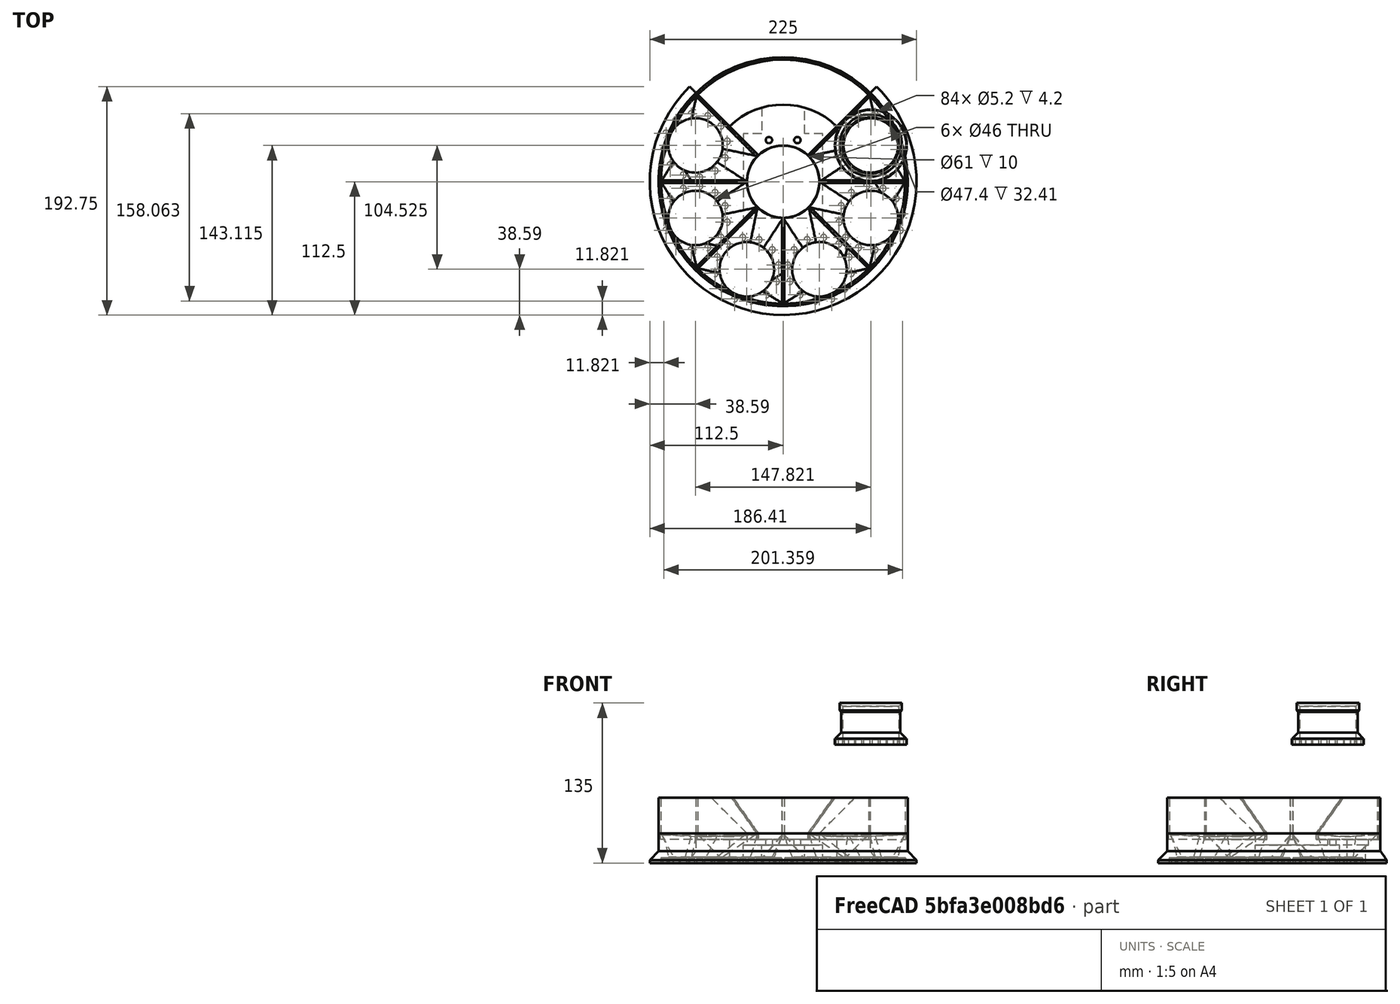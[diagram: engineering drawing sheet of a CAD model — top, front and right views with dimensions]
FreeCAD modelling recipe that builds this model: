
FCSTD DOCUMENT  (FreeCAD 1.0R38806 (Git))
Label: Dust Collector Hose Sorter - Magnetic
License: All rights reserved
LicenseURL: https://en.wikipedia.org/wiki/All_rights_reserved
objects: Sketcher::SketchObject×19, PartDesign::Pocket×9, PartDesign::Pad×7, PartDesign::Chamfer×4, PartDesign::PolarPattern×3, PartDesign::Body×3, Mesh::Feature×2, PartDesign::Groove×1, PartDesign::SubtractiveLoft×1, PartDesign::Boolean×1
note: 115 computed .brp shape members not serialized (recipe doc carries the construction recipe); baked Part::Feature solids carry a one-line shape summary decoded from their .brp

FEATURE [Sketcher::SketchObject] Sketch
  ArcFitTolerance = 1e-06
  AttachmentSupport = -> [XY_Plane]
  FullyConstrained = true
  MakeInternals = false
  MapMode = 5
  sketch-geometry (2):
    g0: Circle CenterX=0 CenterY=0 CenterZ=0 NormalX=0 NormalY=0 NormalZ=1 AngleXU=0 Radius=105
    g1: Circle CenterX=0 CenterY=0 CenterZ=0 NormalX=0 NormalY=0 NormalZ=1 AngleXU=0 Radius=30.5
  constraints (4):
    c: Coincident(g0,g-1)
    c: Diameter(g1) = 61
    c: Coincident(g1,g0)
    c: Diameter(g0) = 210
FEATURE [Sketcher::SketchObject] Sketch012  label="ArmCutout"
  ArcFitTolerance = 1e-06
  FullyConstrained = false
  MakeInternals = false
  MapMode = 5
  sketch-geometry (12):
    g0: LineSegment StartX=33.5 StartY=-30.5 StartZ=0 EndX=33.5 EndY=40.5 EndZ=0
    g1: LineSegment StartX=33.5 StartY=40.5 StartZ=0 EndX=18 EndY=40.5 EndZ=0
    g2: LineSegment StartX=-33.5 StartY=40.5 StartZ=0 EndX=-33.5 EndY=-30.5 EndZ=0
    g3: LineSegment StartX=-33.5 StartY=-30.5 StartZ=0 EndX=33.5 EndY=-30.5 EndZ=0
    g4: GeomPoint [constr] X=0 Y=0 Z=0
    g5: Circle [constr] CenterX=-12 CenterY=35.1 CenterZ=0 NormalX=0 NormalY=0 NormalZ=1 AngleXU=0 Radius=2.7
    g6: Circle [constr] CenterX=12 CenterY=35.1 CenterZ=0 NormalX=0 NormalY=0 NormalZ=1 AngleXU=0 Radius=2.7
    g7: LineSegment StartX=18 StartY=40.5 StartZ=0 EndX=18 EndY=183.45 EndZ=0
    g8: LineSegment StartX=18 StartY=183.45 StartZ=0 EndX=-18 EndY=183.45 EndZ=0
    g9: LineSegment StartX=-18 StartY=183.45 StartZ=0 EndX=-18 EndY=40.5 EndZ=0
    g10: GeomPoint [constr] X=1e-16 Y=15.8458 Z=0
    g11: LineSegment StartX=-18 StartY=40.5 StartZ=0 EndX=-33.5 EndY=40.5 EndZ=0
  constraints (28):
    c: Coincident(g0,g1)
    c: Coincident(g11,g2)
    c: Coincident(g2,g3)
    c: Coincident(g3,g0)
    c: Vertical(g0)
    c: Vertical(g2)
    c: Horizontal(g3)
    c: Coincident(g4,g-1)
    c: DistanceX(g11,g1) = 67
    c: DistanceY(g0,g0) = 71
    c: DistanceY(g2,g4) = 30.5
    c: Symmetric(g11,g0,g-2)
    c: Diameter(g5) = 5.4
    c: Diameter(g6) = 5.4
    c: DistanceX(g5,g6) = 24
    c: DistanceY(g4,g5) = 35.1
    c: Symmetric(g5,g6,g-2)
    c: Coincident(g7,g8)
    c: Coincident(g8,g9)
    c: Vertical(g7)
    c: Vertical(g9)
    c: Horizontal(g8)
    c: PointOnObject(g10,g-2)
    c: DistanceX(g8,g8) = 36
    c: PointOnObject(g9,g11)
    c: Coincident(g1,g7)
    c: PointOnObject(g11,g9)
    c: Symmetric(g9,g1,g-2)
FEATURE [Sketcher::SketchObject] Sketch017  label="ScrewHoles"
  ArcFitTolerance = 1e-06
  FullyConstrained = true
  MakeInternals = false
  MapMode = 5
  sketch-geometry (7):
    g0: LineSegment [constr] StartX=33.5 StartY=-30.5 StartZ=0 EndX=33.5 EndY=40.5 EndZ=0
    g1: LineSegment [constr] StartX=33.5 StartY=40.5 StartZ=0 EndX=-33.5 EndY=40.5 EndZ=0
    g2: LineSegment [constr] StartX=-33.5 StartY=40.5 StartZ=0 EndX=-33.5 EndY=-30.5 EndZ=0
    g3: LineSegment [constr] StartX=-33.5 StartY=-30.5 StartZ=0 EndX=33.5 EndY=-30.5 EndZ=0
    g4: GeomPoint [constr] X=0 Y=0 Z=0
    g5: Circle CenterX=-12 CenterY=35.1 CenterZ=0 NormalX=0 NormalY=0 NormalZ=1 AngleXU=0 Radius=2.7
    g6: Circle CenterX=12 CenterY=35.1 CenterZ=0 NormalX=0 NormalY=0 NormalZ=1 AngleXU=0 Radius=2.7
  constraints (17):
    c: Coincident(g0,g1)
    c: Coincident(g1,g2)
    c: Coincident(g2,g3)
    c: Coincident(g3,g0)
    c: Vertical(g0)
    c: Vertical(g2)
    c: Horizontal(g3)
    c: Coincident(g4,g-1)
    c: DistanceX(g1,g1) = 67
    c: DistanceY(g0,g0) = 71
    c: DistanceY(g2,g4) = 30.5
    c: Symmetric(g1,g0,g-2)
    c: Diameter(g5) = 5.4
    c: Diameter(g6) = 5.4
    c: DistanceX(g5,g6) = 24
    c: DistanceY(g4,g5) = 35.1
    c: Symmetric(g5,g6,g-2)
FEATURE [PartDesign::Pad] Pad  label="BaseBody"
  Direction = (0,0,1)
  Length = 25
  Length2 = 10
  Profile = -> Sketch
  ReferenceAxis = -> Sketch [N_Axis]
  Refine = true
  Suppressed = false
  Type = 0
FEATURE [PartDesign::Pocket] Pocket  label="Arm"
  BaseFeature = -> Pad
  Direction = (0,0,-1)
  Length = 15
  Length2 = 5
  Profile = -> Sketch012
  ReferenceAxis = -> Sketch012 [N_Axis]
  Refine = true
  Reversed = true
  Suppressed = false
  Type = 0
FEATURE [PartDesign::Pocket] Pocket001  label="Screws"
  BaseFeature = -> Pocket
  Direction = (0,0,-1)
  Length = 5
  Length2 = 5
  Midplane = true
  Profile = -> Sketch017
  ReferenceAxis = -> Sketch017 [N_Axis]
  Refine = true
  Suppressed = false
  Type = 1
FEATURE [Sketcher::SketchObject] Sketch027
  ArcFitTolerance = 1e-06
  AttachmentOffset = pos=(0,0,45) rot=(0,0,1;1.96349rad)
  FullyConstrained = true
  MakeInternals = false
  MapMode = 5
  Placement = pos=(0,0,25) rot=(0,0,1;1.96349rad)
  sketch-geometry (8):
    g0: Circle [constr] CenterX=0 CenterY=0 CenterZ=0 NormalX=0 NormalY=0 NormalZ=1 AngleXU=0 Radius=30.5
    g1: ArcOfCircle CenterX=0 CenterY=0 CenterZ=0 NormalX=0 NormalY=0 NormalZ=1 AngleXU=0 Radius=103 StartAngle=4.31969 EndAngle=5.10509
    g2: LineSegment [constr] StartX=0 StartY=0 StartZ=0 EndX=-39.4164 EndY=-95.1596 EndZ=0
    g3: LineSegment [constr] StartX=0 StartY=0 StartZ=0 EndX=39.4164 EndY=-95.1596 EndZ=0
    g4: LineSegment [constr] StartX=-39.4164 StartY=-95.1596 StartZ=0 EndX=39.4164 EndY=-95.1596 EndZ=0
    g5: LineSegment StartX=-11.6718 StartY=-28.1783 StartZ=0 EndX=-39.4164 EndY=-95.1596 EndZ=0
    g6: LineSegment StartX=39.4164 StartY=-95.1596 StartZ=0 EndX=11.6718 EndY=-28.1783 EndZ=0
    g7: ArcOfCircle CenterX=0 CenterY=0 CenterZ=0 NormalX=0 NormalY=0 NormalZ=1 AngleXU=0 Radius=30.5 StartAngle=4.31969 EndAngle=5.10509
  constraints (22):
    c: Diameter(g0) = 61
    c: Coincident(g0,g-1)
    c: Coincident(g1,g0)
    c: Diameter(g1) = 206
    c: Coincident(g2,g0)
    c: Coincident(g3,g0)
    c: Angle(g2,g3) = 0.785398
    c: Coincident(g4,g2)
    c: Coincident(g4,g3)
    c: Horizontal(g4)
    c: PointOnObject(g5,g0)
    c: Coincident(g5,g2)
    c: Coincident(g6,g3)
    c: PointOnObject(g6,g0)
    c: PointOnObject(g5,g2)
    c: PointOnObject(g6,g3)
    c: Coincident(g7,g0)
    c: Equal(g7,g0)
    c: PointOnObject(g7,g2)
    c: PointOnObject(g7,g3)
    c: Coincident(g1,g3)
    c: Coincident(g1,g2)
FEATURE [Sketcher::SketchObject] Sketch028
  ArcFitTolerance = 1e-06
  AttachmentSupport = -> [XZ_Plane005]
  FullyConstrained = false
  MakeInternals = false
  MapMode = 5
  Placement = pos=(0,0,0) rot=(1,0,0;1.5708rad)
  sketch-geometry (4):
    g0: LineSegment StartX=-30.5 StartY=0 StartZ=0 EndX=-103.271 EndY=72.7715 EndZ=0
    g1: LineSegment StartX=-103.271 StartY=72.7715 StartZ=0 EndX=-22.389 EndY=72.7715 EndZ=0
    g2: LineSegment StartX=-22.389 StartY=72.7715 StartZ=0 EndX=-22.389 EndY=0 EndZ=0
    g3: LineSegment StartX=-30.5 StartY=0 StartZ=0 EndX=-22.389 EndY=0 EndZ=0
  constraints (10):
    c: PointOnObject(g0,g-1)
    c: Angle(g-1,g0) = 2.35619
    c: DistanceX(g0,g-1) = 30.5
    c: Coincident(g1,g0)
    c: Horizontal(g1)
    c: Coincident(g2,g1)
    c: Vertical(g2)
    c: PointOnObject(g3,g0)
    c: Coincident(g3,g2)
    c: Horizontal(g3)
FEATURE [Sketcher::SketchObject] Sketch025
  ArcFitTolerance = 1e-06
  AttachmentOffset = pos=(0,0,-5) rot=(0,0,1;0rad)
  AttachmentSupport = -> [XY_Plane005]
  FullyConstrained = true
  MakeInternals = false
  MapMode = 5
  Placement = pos=(0,0,-5) rot=(0,0,1;0rad)
  sketch-geometry (15):
    g0: Circle [constr] CenterX=0 CenterY=0 CenterZ=0 NormalX=0 NormalY=0 NormalZ=1 AngleXU=0 Radius=30.5
    g1: Circle [constr] CenterX=0 CenterY=0 CenterZ=0 NormalX=0 NormalY=0 NormalZ=1 AngleXU=0 Radius=103.5
    g2: LineSegment [constr] StartX=0 StartY=0 StartZ=0 EndX=-31.9833 EndY=-98.4343 EndZ=0
    g3: LineSegment [constr] StartX=0 StartY=0 StartZ=0 EndX=31.9833 EndY=-98.4343 EndZ=0
    g4: LineSegment [constr] StartX=-31.9833 StartY=-98.4343 StartZ=0 EndX=31.9833 EndY=-98.4343 EndZ=0
    g5: LineSegment StartX=-10.3709 StartY=-28.6827 StartZ=0 EndX=-32.9328 EndY=-98.1207 EndZ=0
    g6: LineSegment StartX=-32.9328 StartY=-98.1207 StartZ=0 EndX=-31.0307 EndY=-98.7388 EndZ=0
    g7: LineSegment StartX=-31.0307 StartY=-98.7388 StartZ=0 EndX=-8.46877 EndY=-29.3007 EndZ=0
    g8: LineSegment StartX=-8.46877 StartY=-29.3007 StartZ=0 EndX=-10.3709 EndY=-28.6827 EndZ=0
    g9: GeomPoint X=-9.42502 Y=-29.0072 Z=0
    g10: LineSegment [constr] StartX=9.89926 StartY=-28.8488 StartZ=0 EndX=32.4584 EndY=-98.2787 EndZ=0
    g11: LineSegment [constr] StartX=32.4584 StartY=-98.2787 StartZ=0 EndX=31.5074 EndY=-98.5877 EndZ=0
    g12: LineSegment [constr] StartX=31.5074 StartY=-98.5877 StartZ=0 EndX=8.94821 EndY=-29.1578 EndZ=0
    g13: LineSegment [constr] StartX=8.94821 StartY=-29.1578 StartZ=0 EndX=9.89926 EndY=-28.8488 EndZ=0
    g14: GeomPoint [constr] X=9.42502 Y=-29.0072 Z=0
  constraints (40):
    c: Diameter(g0) = 61
    c: Coincident(g0,g-1)
    c: Diameter(g1) = 207
    c: Coincident(g1,g0)
    c: Coincident(g2,g0)
    c: PointOnObject(g2,g1)
    c: Coincident(g3,g0)
    c: PointOnObject(g3,g1)
    c: Angle(g2,g3) = 0.628319
    c: Coincident(g4,g2)
    c: Coincident(g4,g3)
    c: Horizontal(g4)
    c: Coincident(g6,g5)
    c: Coincident(g8,g7)
    c: Coincident(g8,g5)
    c: PointOnObject(g5,g0)
    c: PointOnObject(g7,g0)
    c: Coincident(g7,g6)
    c: PointOnObject(g5,g1)
    c: PointOnObject(g6,g1)
    c: Distance(g5,g6) = 2
    c: Distance(g7,g5) = 2
    c: PointOnObject(g9,g2)
    c: PointOnObject(g9,g0)
    c: Distance(g5,g9) = 1
    c: Distance(g5,g2) = 1
    c: Coincident(g11,g10)
    c: Coincident(g12,g11)
    c: Coincident(g13,g10)
    c: Distance(g12,g10) = 1
    c: Distance(g11,g10) = 1
    c: Coincident(g12,g13)
    c: PointOnObject(g10,g0)
    c: PointOnObject(g12,g0)
    c: PointOnObject(g10,g1)
    c: PointOnObject(g11,g1)
    c: PointOnObject(g14,g0)
    c: PointOnObject(g14,g3)
    c: Distance(g14,g10) = 0.5
    c: Distance(g10,g3) = 0.5
FEATURE [Sketcher::SketchObject] Sketch026
  ArcFitTolerance = 1e-06
  AttachmentSupport = -> [XY_Plane005]
  FullyConstrained = true
  MakeInternals = false
  MapMode = 5
  sketch-geometry (2):
    g0: Circle CenterX=0 CenterY=0 CenterZ=0 NormalX=0 NormalY=0 NormalZ=1 AngleXU=0 Radius=105
    g1: Circle CenterX=0 CenterY=0 CenterZ=0 NormalX=0 NormalY=0 NormalZ=1 AngleXU=0 Radius=103
  constraints (4):
    c: Diameter(g0) = 210
    c: Coincident(g0,g-1)
    c: Diameter(g1) = 206
    c: Coincident(g1,g0)
FEATURE [PartDesign::Pad] Pad005
  Direction = (0,0,1)
  Length = 30
  Length2 = 10
  Profile = -> Sketch026
  ReferenceAxis = -> Sketch026 [N_Axis]
  Refine = true
  Suppressed = false
  Type = 0
FEATURE [PartDesign::Pad] Pad006
  BaseFeature = -> Pad005
  Direction = (0,0,1)
  Length = 35
  Length2 = 10
  Profile = -> Sketch025
  ReferenceAxis = -> Sketch025 [N_Axis]
  Refine = true
  Suppressed = false
  Type = 0
FEATURE [PartDesign::PolarPattern] PolarPattern001
  Angle = 360
  Axis = -> Sketch025 [N_Axis]
  BaseFeature = -> Pad006
  Mode = 1
  Occurrences = 7
  Offset = 45
  Originals = -> [Pad006]
  Refine = true
  Suppressed = false
  TransformMode = 0
FEATURE [Sketcher::SketchObject] Sketch030
  ArcFitTolerance = 1e-06
  AttachmentOffset = pos=(0,0,0) rot=(0,0,1;-0.314159rad)
  AttachmentSupport = -> [XY_Plane005]
  FullyConstrained = false
  MakeInternals = false
  MapMode = 5
  Placement = pos=(0,0,0) rot=(0,0,1;5.96903rad)
  sketch-geometry (8):
    g0: LineSegment [constr] StartX=-109.281 StartY=0 StartZ=0 EndX=0 EndY=0 EndZ=0
    g1: LineSegment [constr] StartX=0 StartY=0 StartZ=0 EndX=-2.14e-14 EndY=-116.69 EndZ=0
    g2: LineSegment StartX=-266.815 StartY=-1 StartZ=0 EndX=-22.98 EndY=-1 EndZ=0
    g3: LineSegment StartX=-22.98 StartY=-1 StartZ=0 EndX=-1 EndY=-14.8427 EndZ=0
    g4: LineSegment StartX=-1 StartY=-14.8427 StartZ=0 EndX=-1 EndY=-153.677 EndZ=0
    g5: LineSegment [constr] StartX=-1 StartY=-14.8427 StartZ=0 EndX=-2.8e-15 EndY=-14.8427 EndZ=0
    g6: LineSegment StartX=-266.815 StartY=-1 StartZ=0 EndX=-141.723 EndY=-96.8759 EndZ=0
    g7: LineSegment StartX=-141.723 StartY=-96.8759 StartZ=0 EndX=-1 EndY=-153.677 EndZ=0
  constraints (16):
    c: PointOnObject(g0,g-1)
    c: Coincident(g0,g-1)
    c: Coincident(g1,g0)
    c: Angle(g0,g1) = 1.5708
    c: Horizontal(g2)
    c: Coincident(g3,g2)
    c: Coincident(g4,g3)
    c: Parallel(g4,g1)
    c: Coincident(g5,g3)
    c: PointOnObject(g5,g1)
    c: Angle(g4,g5) = 1.5708
    c: Distance(g3,g5) = 1
    c: DistanceY(g2,g0) = 1
    c: Coincident(g6,g2)
    c: Coincident(g7,g6)
    c: Coincident(g7,g4)
FEATURE [PartDesign::Pocket] Pocket004
  BaseFeature = -> PolarPattern001
  Direction = (0,0,-1)
  Length = 30
  Length2 = 5
  Profile = -> Sketch030
  ReferenceAxis = -> Sketch030 [N_Axis]
  Refine = true
  Reversed = true
  Suppressed = false
  Type = 0
FEATURE [PartDesign::Groove] Groove
  Angle = 360
  Angle2 = 60
  Axis = (0,2e-16,1)
  Base = (0,0,0)
  BaseFeature = -> Pocket004
  Profile = -> Sketch028
  ReferenceAxis = -> Sketch028 [V_Axis]
  Refine = true
  Reversed = true
  Suppressed = false
  Type = 0
FEATURE [Sketcher::SketchObject] Sketch031
  ArcFitTolerance = 1e-06
  AttachmentSupport = -> [XY_Plane005]
  FullyConstrained = true
  MakeInternals = false
  MapMode = 5
  sketch-geometry (1):
    g0: Circle CenterX=0 CenterY=0 CenterZ=0 NormalX=0 NormalY=0 NormalZ=1 AngleXU=0 Radius=30.5
  constraints (2):
    c: Diameter(g0) = 61
    c: Coincident(g0,g-1)
FEATURE [PartDesign::Pocket] Pocket005
  BaseFeature = -> Groove
  Direction = (0,0,-1)
  Length = 5
  Length2 = 5
  Midplane = true
  Profile = -> Sketch031
  ReferenceAxis = -> Sketch031 [N_Axis]
  Refine = true
  Suppressed = false
  Type = 1
FEATURE [PartDesign::Body] Body005  label="Splitter"
  AllowCompound = false
  Group = -> [Sketch025,Sketch026,Pad005,Pad006,PolarPattern001,Sketch030,Pocket004,Sketch028,Groove,Sketch031,Pocket005]
  Origin = -> Origin005
  Placement = pos=(0,0,25) rot=(0,0,1;-2.04203rad)
  Tip = -> Pocket005
FEATURE [Mesh::Feature] CS7_1_Sorter_Base_8_Slot_Ramp  label="CS7.1 Sorter Base 8 Slot Ramp"
  Placement = pos=(28.65,-111,29) rot=(0,0,1;0rad)
FEATURE [Sketcher::SketchObject] Sketch020
  ArcFitTolerance = 1e-06
  AttachmentOffset = pos=(0,0,5) rot=(0,0,1;1.96349rad)
  AttachmentSupport = -> [XY_Plane]
  FullyConstrained = true
  MakeInternals = false
  MapMode = 5
  Placement = pos=(0,0,5) rot=(0,0,1;1.96349rad)
  sketch-geometry (2):
    g0: Circle CenterX=0 CenterY=-80 CenterZ=0 NormalX=0 NormalY=0 NormalZ=1 AngleXU=0 Radius=23
    g1: Circle [constr] CenterX=0 CenterY=0 CenterZ=0 NormalX=0 NormalY=0 NormalZ=1 AngleXU=0 Radius=105
  constraints (5):
    c: Diameter(g0) = 46
    c: PointOnObject(g0,g-2)
    c: DistanceY(g0,g-1) = 80
    c: Diameter(g1) = 210
    c: Coincident(g1,g-1)
FEATURE [PartDesign::SubtractiveLoft] SubtractiveLoft
  BaseFeature = -> Pocket001
  Closed = false
  Profile = -> Sketch027
  Refine = true
  Ruled = true
  Sections = -> [Sketch020]
  Suppressed = false
FEATURE [Sketcher::SketchObject] Sketch034
  ArcFitTolerance = 1e-06
  AttachmentOffset = pos=(0,0,25) rot=(0,0,1;-2.35619rad)
  AttachmentSupport = -> [XY_Plane]
  FullyConstrained = false
  MakeInternals = false
  MapMode = 5
  Placement = pos=(0,0,25) rot=(0,0,1;3.92699rad)
  sketch-geometry (8):
    g0: LineSegment [constr] StartX=-109.281 StartY=0 StartZ=0 EndX=0 EndY=0 EndZ=0
    g1: LineSegment [constr] StartX=0 StartY=0 StartZ=0 EndX=-2.14e-14 EndY=-116.69 EndZ=0
    g2: LineSegment StartX=-266.815 StartY=-1 StartZ=0 EndX=-22.98 EndY=-1 EndZ=0
    g3: LineSegment StartX=-22.98 StartY=-1 StartZ=0 EndX=-1 EndY=-14.8427 EndZ=0
    g4: LineSegment StartX=-1 StartY=-14.8427 StartZ=0 EndX=-1 EndY=-153.677 EndZ=0
    g5: LineSegment [constr] StartX=-1 StartY=-14.8427 StartZ=0 EndX=-2.7e-15 EndY=-14.8427 EndZ=0
    g6: LineSegment StartX=-266.815 StartY=-1 StartZ=0 EndX=-141.723 EndY=-96.8759 EndZ=0
    g7: LineSegment StartX=-141.723 StartY=-96.8759 StartZ=0 EndX=-1 EndY=-153.677 EndZ=0
  constraints (16):
    c: PointOnObject(g0,g-1)
    c: Coincident(g0,g-1)
    c: Coincident(g1,g0)
    c: Angle(g0,g1) = 1.5708
    c: Horizontal(g2)
    c: Coincident(g3,g2)
    c: Coincident(g4,g3)
    c: Parallel(g4,g1)
    c: Coincident(g5,g3)
    c: PointOnObject(g5,g1)
    c: Angle(g4,g5) = 1.5708
    c: Distance(g3,g5) = 1
    c: DistanceY(g2,g0) = 1
    c: Coincident(g6,g2)
    c: Coincident(g7,g6)
    c: Coincident(g7,g4)
FEATURE [Sketcher::SketchObject] Sketch035
  ArcFitTolerance = 1e-06
  AttachmentOffset = pos=(0,0,35) rot=(0,0,1;-2.35619rad)
  AttachmentSupport = -> [XY_Plane]
  FullyConstrained = false
  MakeInternals = false
  MapMode = 5
  Placement = pos=(0,0,35) rot=(0,0,1;3.92699rad)
  sketch-geometry (8):
    g0: LineSegment [constr] StartX=-109.281 StartY=0 StartZ=0 EndX=0 EndY=0 EndZ=0
    g1: LineSegment [constr] StartX=0 StartY=0 StartZ=0 EndX=-2.14e-14 EndY=-116.69 EndZ=0
    g2: LineSegment StartX=-266.815 StartY=-1.00016 StartZ=0 EndX=-64.9923 EndY=-1.00016 EndZ=0
    g3: LineSegment StartX=-1.00017 StartY=-64.9923 StartZ=0 EndX=-1.00017 EndY=-153.677 EndZ=0
    g4: LineSegment [constr] StartX=-1 StartY=-14.8427 StartZ=0 EndX=-2.7e-15 EndY=-14.8427 EndZ=0
    g5: LineSegment StartX=-266.815 StartY=-1.00016 StartZ=0 EndX=-141.723 EndY=-96.8759 EndZ=0
    g6: LineSegment StartX=-141.723 StartY=-96.8759 StartZ=0 EndX=-1.00017 EndY=-153.677 EndZ=0
    g7: ArcOfCircle CenterX=0 CenterY=0 CenterZ=0 NormalX=0 NormalY=0 NormalZ=1 AngleXU=0 Radius=65 StartAngle=3.15698 EndAngle=4.697
  constraints (15):
    c: PointOnObject(g0,g-1)
    c: Coincident(g0,g-1)
    c: Coincident(g1,g0)
    c: Angle(g0,g1) = 1.5708
    c: Horizontal(g2)
    c: Parallel(g3,g1)
    c: PointOnObject(g4,g1)
    c: Angle(g3,g4) = 1.5708
    c: Coincident(g5,g2)
    c: Coincident(g6,g5)
    c: Coincident(g6,g3)
    c: Coincident(g7,g0)
    c: Diameter(g7) = 130
    c: Coincident(g7,g3)
    c: Coincident(g7,g2)
FEATURE [Mesh::Feature] CS7_1_Sorter_Base  label="CS7.1 Sorter Base"
  Placement = pos=(-2,63,39) rot=(0,0,-1;1.5708rad)
FEATURE [Sketcher::SketchObject] Sketch036
  ArcFitTolerance = 1e-06
  AttachmentOffset = pos=(0,0,5) rot=(0,0,1;1.96349rad)
  AttachmentSupport = -> [XY_Plane]
  FullyConstrained = true
  MakeInternals = false
  MapMode = 5
  Placement = pos=(0,0,5) rot=(0,0,1;1.96349rad)
  sketch-geometry (2):
    g0: Circle CenterX=0 CenterY=-80 CenterZ=0 NormalX=0 NormalY=0 NormalZ=1 AngleXU=0 Radius=23
    g1: Circle [constr] CenterX=0 CenterY=0 CenterZ=0 NormalX=0 NormalY=0 NormalZ=1 AngleXU=0 Radius=105
  constraints (5):
    c: Diameter(g0) = 46
    c: PointOnObject(g0,g-2)
    c: DistanceY(g0,g-1) = 80
    c: Diameter(g1) = 210
    c: Coincident(g1,g-1)
FEATURE [PartDesign::Pocket] Pocket009
  BaseFeature = -> SubtractiveLoft
  Direction = (0,0,-1)
  Length = 5
  Length2 = 5
  Profile = -> Sketch036
  ReferenceAxis = -> Sketch036 [N_Axis]
  Refine = true
  Suppressed = false
  Type = 0
FEATURE [PartDesign::PolarPattern] PolarPattern
  Angle = 360
  Axis = -> Sketch027 [N_Axis]
  BaseFeature = -> Pocket009
  Mode = 1
  Occurrences = 6
  Offset = 45
  Originals = -> [SubtractiveLoft,Pocket009]
  Refine = true
  Reversed = true
  Suppressed = false
  TransformMode = 0
FEATURE [PartDesign::Boolean] Boolean
  BaseFeature = -> PolarPattern
  Group = -> [Body005]
  Refine = true
  Suppressed = false
  Type = 0
  UsePlacement = true
FEATURE [Sketcher::SketchObject] Sketch037
  ArcFitTolerance = 1e-06
  AttachmentSupport = -> [XY_Plane]
  FullyConstrained = true
  MakeInternals = false
  MapMode = 5
  sketch-geometry (2):
    g0: Circle CenterX=0 CenterY=0 CenterZ=0 NormalX=0 NormalY=0 NormalZ=1 AngleXU=0 Radius=105
    g1: Circle CenterX=0 CenterY=0 CenterZ=0 NormalX=0 NormalY=0 NormalZ=1 AngleXU=0 Radius=112.5
  constraints (4):
    c: Diameter(g0) = 210
    c: Coincident(g0,g-1)
    c: Diameter(g1) = 225
    c: Coincident(g1,g0)
FEATURE [PartDesign::Pad] Pad007  label="Magnet Ring"
  BaseFeature = -> Boolean
  Direction = (0,0,1)
  Length = 10
  Length2 = 10
  Profile = -> Sketch037
  ReferenceAxis = -> Sketch037 [N_Axis]
  Refine = true
  Suppressed = false
  Type = 0
FEATURE [PartDesign::Pocket] Pocket007
  BaseFeature = -> Pad007
  Direction = (0,0,-1)
  Length = 5
  Length2 = 5
  Profile = -> Sketch034
  ReferenceAxis = -> Sketch034 [N_Axis]
  Refine = true
  Suppressed = false
  Type = 0
FEATURE [PartDesign::Pocket] Pocket008
  BaseFeature = -> Pocket007
  Direction = (0,0,-1)
  Length = 5
  Length2 = 5
  Midplane = true
  Profile = -> Sketch035
  ReferenceAxis = -> Sketch035 [N_Axis]
  Refine = true
  Suppressed = false
  Type = 1
FEATURE [Sketcher::SketchObject] Sketch038
  ArcFitTolerance = 1e-06
  AttachmentOffset = pos=(0,0,0) rot=(0,0,1;1.96349rad)
  AttachmentSupport = -> [XY_Plane]
  FullyConstrained = true
  MakeInternals = false
  MapMode = 5
  Placement = pos=(0,0,0) rot=(0,0,1;1.96349rad)
  sketch-geometry (39):
    g0: Circle [constr] CenterX=0 CenterY=-80 CenterZ=0 NormalX=0 NormalY=0 NormalZ=1 AngleXU=0 Radius=24
    g1: Circle [constr] CenterX=0 CenterY=-80 CenterZ=0 NormalX=0 NormalY=0 NormalZ=1 AngleXU=0 Radius=24
    g2: Circle [constr] CenterX=0 CenterY=-80 CenterZ=0 NormalX=0 NormalY=0 NormalZ=1 AngleXU=0 Radius=30
    g3: LineSegment [constr] StartX=0 StartY=-50 StartZ=0 EndX=0 EndY=-56 EndZ=0
    g4: Circle CenterX=0 CenterY=-53 CenterZ=0 NormalX=0 NormalY=0 NormalZ=1 AngleXU=0 Radius=2.6
    g5: LineSegment [constr] StartX=0 StartY=-50 StartZ=0 EndX=0 EndY=-80 EndZ=0
    g6: LineSegment [constr] StartX=0 StartY=-80 StartZ=0 EndX=25.9808 EndY=-65 EndZ=0
    g7: LineSegment [constr] StartX=0 StartY=-80 StartZ=0 EndX=25.9807 EndY=-95 EndZ=0
    g8: LineSegment [constr] StartX=0 StartY=-80 StartZ=0 EndX=-4.03923e-05 EndY=-110 EndZ=0
    g9: LineSegment [constr] StartX=0 StartY=-80 StartZ=0 EndX=-25.9808 EndY=-95 EndZ=0
    g10: LineSegment [constr] StartX=0 StartY=-80 StartZ=0 EndX=-25.9807 EndY=-64.9999 EndZ=0
    g11: GeomPoint [constr] X=20.7846 Y=-68 Z=0
    g12: GeomPoint [constr] X=20.7846 Y=-92 Z=0
    g13: GeomPoint [constr] X=-3.23138e-05 Y=-104 Z=0
    g14: GeomPoint [constr] X=-20.7846 Y=-92 Z=0
    g15: GeomPoint [constr] X=-20.7846 Y=-68 Z=0
    g16: Circle CenterX=-23.3827 CenterY=-66.4999 CenterZ=0 NormalX=0 NormalY=0 NormalZ=1 AngleXU=0 Radius=2.6
    g17: Circle CenterX=-23.3827 CenterY=-93.5 CenterZ=0 NormalX=0 NormalY=0 NormalZ=1 AngleXU=0 Radius=2.6
    g18: Circle CenterX=-3.63531e-05 CenterY=-107 CenterZ=0 NormalX=0 NormalY=0 NormalZ=1 AngleXU=0 Radius=2.6
    g19: Circle CenterX=23.3827 CenterY=-93.5 CenterZ=0 NormalX=0 NormalY=0 NormalZ=1 AngleXU=0 Radius=2.6
    g20: Circle CenterX=23.3827 CenterY=-66.5 CenterZ=0 NormalX=0 NormalY=0 NormalZ=1 AngleXU=0 Radius=2.6
    g21: LineSegment [constr] StartX=0 StartY=-80 StartZ=0 EndX=15 EndY=-54.0192 EndZ=0
    g22: LineSegment [constr] StartX=0 StartY=-80 StartZ=0 EndX=30 EndY=-80 EndZ=0
    g23: LineSegment [constr] StartX=0 StartY=-80 StartZ=0 EndX=15 EndY=-105.981 EndZ=0
    g24: LineSegment [constr] StartX=0 StartY=-80 StartZ=0 EndX=-15 EndY=-105.981 EndZ=0
    g25: LineSegment [constr] StartX=0 StartY=-80 StartZ=0 EndX=-30 EndY=-79.9999 EndZ=0
    g26: LineSegment [constr] StartX=0 StartY=-80 StartZ=0 EndX=-14.9999 EndY=-54.0192 EndZ=0
    g27: Circle CenterX=-13.4999 CenterY=-56.6173 CenterZ=0 NormalX=0 NormalY=0 NormalZ=1 AngleXU=0 Radius=2.6
    g28: Circle CenterX=-27 CenterY=-79.9999 CenterZ=0 NormalX=0 NormalY=0 NormalZ=1 AngleXU=0 Radius=2.6
    g29: Circle CenterX=-13.5 CenterY=-103.383 CenterZ=0 NormalX=0 NormalY=0 NormalZ=1 AngleXU=0 Radius=2.6
    g30: Circle CenterX=13.5 CenterY=-103.383 CenterZ=0 NormalX=0 NormalY=0 NormalZ=1 AngleXU=0 Radius=2.6
    g31: Circle CenterX=27 CenterY=-80 CenterZ=0 NormalX=0 NormalY=0 NormalZ=1 AngleXU=0 Radius=2.6
    g32: Circle CenterX=13.5 CenterY=-56.6173 CenterZ=0 NormalX=0 NormalY=0 NormalZ=1 AngleXU=0 Radius=2.6
    g33: GeomPoint X=-12 Y=-100.785 Z=0
    g34: GeomPoint X=-24 Y=-80 Z=0
    g35: GeomPoint X=-11.9999 Y=-59.2154 Z=0
    g36: GeomPoint X=12 Y=-59.2154 Z=0
    g37: GeomPoint X=24 Y=-80 Z=0
    g38: GeomPoint X=12 Y=-100.785 Z=0
  constraints (92):
    c: Diameter(g0) = 48
    c: PointOnObject(g0,g-2)
    c: DistanceY(g0,g-1) = 80
    c: Diameter(g1) = 48
    c: Coincident(g1,g0)
    c: Diameter(g2) = 60
    c: Coincident(g2,g0)
    c: PointOnObject(g3,g2)
    c: PointOnObject(g3,g1)
    c: Vertical(g3)
    c: PointOnObject(g3,g-2)
    c: Diameter(g4) = 5.2
    c: Symmetric(g3,g3,g4)
    c: Coincident(g5,g3)
    c: Coincident(g5,g0)
    c: Coincident(g6,g0)
    c: Angle(g6,g5) = 1.0472
    c: Coincident(g7,g0)
    c: Coincident(g8,g0)
    c: Coincident(g9,g0)
    c: Coincident(g10,g0)
    c: Angle(g7,g6) = 1.0472
    c: Angle(g8,g7) = 1.0472
    c: Angle(g9,g8) = 1.0472
    c: Angle(g10,g9) = 1.0472
    c: PointOnObject(g10,g2)
    c: PointOnObject(g9,g2)
    c: PointOnObject(g8,g2)
    c: PointOnObject(g7,g2)
    c: PointOnObject(g6,g2)
    c: PointOnObject(g11,g1)
    c: PointOnObject(g12,g1)
    c: PointOnObject(g13,g8)
    c: PointOnObject(g14,g9)
    c: PointOnObject(g15,g10)
    c: PointOnObject(g13,g1)
    c: PointOnObject(g14,g1)
    c: PointOnObject(g12,g7)
    c: PointOnObject(g11,g6)
    c: PointOnObject(g15,g1)
    c: Equal(g4,g20)
    c: Equal(g20,g19)
    c: Equal(g19,g18)
    c: Equal(g18,g17)
    c: Equal(g17,g16)
    c: Symmetric(g11,g6,g20)
    c: Symmetric(g12,g7,g19)
    c: Symmetric(g13,g8,g18)
    c: Symmetric(g14,g9,g17)
    c: Symmetric(g10,g15,g16)
    c: Coincident(g21,g0)
    c: PointOnObject(g21,g2)
    c: Coincident(g22,g0)
    c: PointOnObject(g22,g2)
    c: Coincident(g23,g0)
    c: PointOnObject(g23,g2)
    c: Coincident(g24,g0)
    c: PointOnObject(g24,g2)
    c: Coincident(g25,g0)
    c: PointOnObject(g25,g2)
    c: Angle(g6,g21) = 0.523599
    c: Angle(g7,g22) = 0.523599
    c: Angle(g8,g23) = 0.523599
    c: Angle(g24,g8) = 0.523599
    c: Angle(g25,g9) = 0.523599
    c: PointOnObject(g26,g2)
    c: Angle(g26,g10) = 0.523599
    c: Coincident(g26,g1)
    c: PointOnObject(g27,g26)
    c: PointOnObject(g28,g25)
    c: PointOnObject(g29,g24)
    c: PointOnObject(g30,g23)
    c: PointOnObject(g31,g22)
    c: PointOnObject(g32,g21)
    c: Equal(g32,g20)
    c: Equal(g32,g27)
    c: Equal(g16,g28)
    c: Equal(g17,g29)
    c: Equal(g18,g30)
    c: Equal(g31,g19)
    c: PointOnObject(g33,g0)
    c: PointOnObject(g34,g0)
    c: PointOnObject(g35,g0)
    c: PointOnObject(g38,g0)
    c: PointOnObject(g37,g0)
    c: PointOnObject(g36,g0)
    c: Symmetric(g38,g23,g30)
    c: Symmetric(g22,g37,g31)
    c: Symmetric(g21,g36,g32)
    c: Symmetric(g26,g35,g27)
    c: Symmetric(g25,g34,g28)
    c: Symmetric(g33,g24,g29)
FEATURE [PartDesign::Pocket] Pocket010
  BaseFeature = -> Pocket008
  Direction = (0,0,-1)
  Length = 4.2
  Length2 = 5
  Profile = -> Sketch038
  ReferenceAxis = -> Sketch038 [N_Axis]
  Refine = true
  Reversed = true
  Suppressed = false
  Type = 0
FEATURE [PartDesign::PolarPattern] PolarPattern002
  Angle = 360
  Axis = -> Sketch038 [N_Axis]
  BaseFeature = -> Pocket010
  Mode = 1
  Occurrences = 6
  Offset = 45
  Originals = -> [Pocket010]
  Refine = true
  Reversed = true
  Suppressed = false
  TransformMode = 0
FEATURE [Sketcher::SketchObject] Sketch039
  ArcFitTolerance = 1e-06
  AttachmentOffset = pos=(0,0,0) rot=(0,0,1;1.96349rad)
  AttachmentSupport = -> [XY_Plane006]
  FullyConstrained = true
  MakeInternals = false
  MapMode = 5
  Placement = pos=(0,0,0) rot=(0,0,1;1.96349rad)
  sketch-geometry (21):
    g0: Circle CenterX=0 CenterY=-80 CenterZ=0 NormalX=0 NormalY=0 NormalZ=1 AngleXU=0 Radius=23.7
    g1: Circle [constr] CenterX=0 CenterY=-80 CenterZ=0 NormalX=0 NormalY=0 NormalZ=1 AngleXU=0 Radius=24
    g2: Circle CenterX=0 CenterY=-80 CenterZ=0 NormalX=0 NormalY=0 NormalZ=1 AngleXU=0 Radius=30.3
    g3: LineSegment [constr] StartX=0 StartY=-49.7 StartZ=0 EndX=0 EndY=-56 EndZ=0
    g4: Circle [constr] CenterX=0 CenterY=-52.85 CenterZ=0 NormalX=0 NormalY=0 NormalZ=1 AngleXU=0 Radius=2.6
    g5: LineSegment [constr] StartX=0 StartY=-49.7 StartZ=0 EndX=0 EndY=-80 EndZ=0
    g6: LineSegment [constr] StartX=0 StartY=-80 StartZ=0 EndX=26.2406 EndY=-64.85 EndZ=0
    g7: LineSegment [constr] StartX=0 StartY=-80 StartZ=0 EndX=26.2406 EndY=-95.15 EndZ=0
    g8: LineSegment [constr] StartX=0 StartY=-80 StartZ=0 EndX=1.18e-14 EndY=-110.3 EndZ=0
    g9: LineSegment [constr] StartX=0 StartY=-80 StartZ=0 EndX=-26.2406 EndY=-95.15 EndZ=0
    g10: LineSegment [constr] StartX=0 StartY=-80 StartZ=0 EndX=-26.2406 EndY=-64.85 EndZ=0
    g11: GeomPoint [constr] X=20.7846 Y=-68 Z=0
    g12: GeomPoint [constr] X=20.7846 Y=-92 Z=0
    g13: GeomPoint [constr] X=9.4e-15 Y=-104 Z=0
    g14: GeomPoint [constr] X=-20.7846 Y=-92 Z=0
    g15: GeomPoint [constr] X=-20.7846 Y=-68 Z=0
    g16: Circle [constr] CenterX=-23.5126 CenterY=-66.425 CenterZ=0 NormalX=0 NormalY=0 NormalZ=1 AngleXU=0 Radius=2.6
    g17: Circle [constr] CenterX=-23.5126 CenterY=-93.575 CenterZ=0 NormalX=0 NormalY=0 NormalZ=1 AngleXU=0 Radius=2.6
    g18: Circle [constr] CenterX=1.06e-14 CenterY=-107.15 CenterZ=0 NormalX=0 NormalY=0 NormalZ=1 AngleXU=0 Radius=2.6
    g19: Circle [constr] CenterX=23.5126 CenterY=-93.575 CenterZ=0 NormalX=0 NormalY=0 NormalZ=1 AngleXU=0 Radius=2.6
    g20: Circle [constr] CenterX=23.5126 CenterY=-66.425 CenterZ=0 NormalX=0 NormalY=0 NormalZ=1 AngleXU=0 Radius=2.6
  constraints (50):
    c: Diameter(g0) = 47.4
    c: PointOnObject(g0,g-2)
    c: DistanceY(g0,g-1) = 80
    c: Diameter(g1) = 48
    c: Coincident(g1,g0)
    c: Diameter(g2) = 60.6
    c: Coincident(g2,g0)
    c: PointOnObject(g3,g2)
    c: PointOnObject(g3,g1)
    c: Vertical(g3)
    c: PointOnObject(g3,g-2)
    c: Diameter(g4) = 5.2
    c: Symmetric(g3,g3,g4)
    c: Coincident(g5,g3)
    c: Coincident(g5,g0)
    c: Coincident(g6,g0)
    c: Angle(g6,g5) = 1.0472
    c: Coincident(g7,g0)
    c: Coincident(g8,g0)
    c: Coincident(g9,g0)
    c: Coincident(g10,g0)
    c: Angle(g7,g6) = 1.0472
    c: Angle(g8,g7) = 1.0472
    c: Angle(g9,g8) = 1.0472
    c: Angle(g10,g9) = 1.0472
    c: PointOnObject(g10,g2)
    c: PointOnObject(g9,g2)
    c: PointOnObject(g8,g2)
    c: PointOnObject(g7,g2)
    c: PointOnObject(g6,g2)
    c: PointOnObject(g11,g1)
    c: PointOnObject(g12,g1)
    c: PointOnObject(g13,g8)
    c: PointOnObject(g14,g9)
    c: PointOnObject(g15,g10)
    c: PointOnObject(g13,g1)
    c: PointOnObject(g14,g1)
    c: PointOnObject(g12,g7)
    c: PointOnObject(g11,g6)
    c: PointOnObject(g15,g1)
    c: Equal(g4,g20)
    c: Equal(g20,g19)
    c: Equal(g19,g18)
    c: Equal(g18,g17)
    c: Equal(g17,g16)
    c: Symmetric(g11,g6,g20)
    c: Symmetric(g12,g7,g19)
    c: Symmetric(g13,g8,g18)
    c: Symmetric(g14,g9,g17)
    c: Symmetric(g10,g15,g16)
FEATURE [PartDesign::Pad] Pad008
  Direction = (0,0,1)
  Length = 5
  Length2 = 10
  Profile = -> Sketch039
  ReferenceAxis = -> Sketch039 [N_Axis]
  Refine = true
  Suppressed = false
  Type = 0
FEATURE [Sketcher::SketchObject] Sketch040
  ArcFitTolerance = 1e-06
  AttachmentOffset = pos=(0,0,0) rot=(0,0,1;1.96349rad)
  AttachmentSupport = -> [XY_Plane006]
  FullyConstrained = true
  MakeInternals = false
  MapMode = 5
  Placement = pos=(0,0,0) rot=(0,0,1;1.96349rad)
  sketch-geometry (39):
    g0: Circle [constr] CenterX=0 CenterY=-80 CenterZ=0 NormalX=0 NormalY=0 NormalZ=1 AngleXU=0 Radius=24
    g1: Circle [constr] CenterX=0 CenterY=-80 CenterZ=0 NormalX=0 NormalY=0 NormalZ=1 AngleXU=0 Radius=24
    g2: Circle [constr] CenterX=0 CenterY=-80 CenterZ=0 NormalX=0 NormalY=0 NormalZ=1 AngleXU=0 Radius=30
    g3: LineSegment [constr] StartX=0 StartY=-50 StartZ=0 EndX=0 EndY=-56 EndZ=0
    g4: Circle CenterX=0 CenterY=-53 CenterZ=0 NormalX=0 NormalY=0 NormalZ=1 AngleXU=0 Radius=2.6
    g5: LineSegment [constr] StartX=0 StartY=-50 StartZ=0 EndX=0 EndY=-80 EndZ=0
    g6: LineSegment [constr] StartX=0 StartY=-80 StartZ=0 EndX=25.9808 EndY=-65 EndZ=0
    g7: LineSegment [constr] StartX=0 StartY=-80 StartZ=0 EndX=25.9808 EndY=-95 EndZ=0
    g8: LineSegment [constr] StartX=0 StartY=-80 StartZ=0 EndX=7.4e-15 EndY=-110 EndZ=0
    g9: LineSegment [constr] StartX=0 StartY=-80 StartZ=0 EndX=-25.9808 EndY=-95 EndZ=0
    g10: LineSegment [constr] StartX=0 StartY=-80 StartZ=0 EndX=-25.9808 EndY=-65 EndZ=0
    g11: GeomPoint [constr] X=20.7846 Y=-68 Z=0
    g12: GeomPoint [constr] X=20.7846 Y=-92 Z=0
    g13: GeomPoint [constr] X=5.9e-15 Y=-104 Z=0
    g14: GeomPoint [constr] X=-20.7846 Y=-92 Z=0
    g15: GeomPoint [constr] X=-20.7846 Y=-68 Z=0
    g16: Circle CenterX=-23.3827 CenterY=-66.5 CenterZ=0 NormalX=0 NormalY=0 NormalZ=1 AngleXU=0 Radius=2.6
    g17: Circle CenterX=-23.3827 CenterY=-93.5 CenterZ=0 NormalX=0 NormalY=0 NormalZ=1 AngleXU=0 Radius=2.6
    g18: Circle CenterX=6.6e-15 CenterY=-107 CenterZ=0 NormalX=0 NormalY=0 NormalZ=1 AngleXU=0 Radius=2.6
    g19: Circle CenterX=23.3827 CenterY=-93.5 CenterZ=0 NormalX=0 NormalY=0 NormalZ=1 AngleXU=0 Radius=2.6
    g20: Circle CenterX=23.3827 CenterY=-66.5 CenterZ=0 NormalX=0 NormalY=0 NormalZ=1 AngleXU=0 Radius=2.6
    g21: LineSegment [constr] StartX=0 StartY=-80 StartZ=0 EndX=15 EndY=-54.0192 EndZ=0
    g22: LineSegment [constr] StartX=0 StartY=-80 StartZ=0 EndX=30 EndY=-80 EndZ=0
    g23: LineSegment [constr] StartX=0 StartY=-80 StartZ=0 EndX=15 EndY=-105.981 EndZ=0
    g24: LineSegment [constr] StartX=0 StartY=-80 StartZ=0 EndX=-15 EndY=-105.981 EndZ=0
    g25: LineSegment [constr] StartX=0 StartY=-80 StartZ=0 EndX=-30 EndY=-80 EndZ=0
    g26: LineSegment [constr] StartX=0 StartY=-80 StartZ=0 EndX=-15 EndY=-54.0192 EndZ=0
    g27: Circle CenterX=-13.5 CenterY=-56.6173 CenterZ=0 NormalX=0 NormalY=0 NormalZ=1 AngleXU=0 Radius=2.6
    g28: Circle CenterX=-27 CenterY=-80 CenterZ=0 NormalX=0 NormalY=0 NormalZ=1 AngleXU=0 Radius=2.6
    g29: Circle CenterX=-13.5 CenterY=-103.383 CenterZ=0 NormalX=0 NormalY=0 NormalZ=1 AngleXU=0 Radius=2.6
    g30: Circle CenterX=13.5 CenterY=-103.383 CenterZ=0 NormalX=0 NormalY=0 NormalZ=1 AngleXU=0 Radius=2.6
    g31: Circle CenterX=27 CenterY=-80 CenterZ=0 NormalX=0 NormalY=0 NormalZ=1 AngleXU=0 Radius=2.6
    g32: Circle CenterX=13.5 CenterY=-56.6173 CenterZ=0 NormalX=0 NormalY=0 NormalZ=1 AngleXU=0 Radius=2.6
    g33: GeomPoint X=-12 Y=-100.785 Z=0
    g34: GeomPoint X=-24 Y=-80 Z=0
    g35: GeomPoint X=-12 Y=-59.2154 Z=0
    g36: GeomPoint X=12 Y=-59.2154 Z=0
    g37: GeomPoint X=24 Y=-80 Z=0
    g38: GeomPoint X=12 Y=-100.785 Z=0
  constraints (92):
    c: Diameter(g0) = 48
    c: PointOnObject(g0,g-2)
    c: DistanceY(g0,g-1) = 80
    c: Diameter(g1) = 48
    c: Coincident(g1,g0)
    c: Diameter(g2) = 60
    c: Coincident(g2,g0)
    c: PointOnObject(g3,g2)
    c: PointOnObject(g3,g1)
    c: Vertical(g3)
    c: PointOnObject(g3,g-2)
    c: Diameter(g4) = 5.2
    c: Symmetric(g3,g3,g4)
    c: Coincident(g5,g3)
    c: Coincident(g5,g0)
    c: Coincident(g6,g0)
    c: Angle(g6,g5) = 1.0472
    c: Coincident(g7,g0)
    c: Coincident(g8,g0)
    c: Coincident(g9,g0)
    c: Coincident(g10,g0)
    c: Angle(g7,g6) = 1.0472
    c: Angle(g8,g7) = 1.0472
    c: Angle(g9,g8) = 1.0472
    c: Angle(g10,g9) = 1.0472
    c: PointOnObject(g10,g2)
    c: PointOnObject(g9,g2)
    c: PointOnObject(g8,g2)
    c: PointOnObject(g7,g2)
    c: PointOnObject(g6,g2)
    c: PointOnObject(g11,g1)
    c: PointOnObject(g12,g1)
    c: PointOnObject(g13,g8)
    c: PointOnObject(g14,g9)
    c: PointOnObject(g15,g10)
    c: PointOnObject(g13,g1)
    c: PointOnObject(g14,g1)
    c: PointOnObject(g12,g7)
    c: PointOnObject(g11,g6)
    c: PointOnObject(g15,g1)
    c: Equal(g4,g20)
    c: Equal(g20,g19)
    c: Equal(g19,g18)
    c: Equal(g18,g17)
    c: Equal(g17,g16)
    c: Symmetric(g11,g6,g20)
    c: Symmetric(g12,g7,g19)
    c: Symmetric(g13,g8,g18)
    c: Symmetric(g14,g9,g17)
    c: Symmetric(g10,g15,g16)
    c: Coincident(g21,g0)
    c: PointOnObject(g21,g2)
    c: Coincident(g22,g0)
    c: PointOnObject(g22,g2)
    c: Coincident(g23,g0)
    c: PointOnObject(g23,g2)
    c: Coincident(g24,g0)
    c: PointOnObject(g24,g2)
    c: Coincident(g25,g0)
    c: PointOnObject(g25,g2)
    c: Angle(g6,g21) = 0.523599
    c: Angle(g7,g22) = 0.523599
    c: Angle(g8,g23) = 0.523599
    c: Angle(g24,g8) = 0.523599
    c: Angle(g25,g9) = 0.523599
    c: PointOnObject(g26,g2)
    c: Angle(g26,g10) = 0.523599
    c: Coincident(g26,g1)
    c: PointOnObject(g27,g26)
    c: PointOnObject(g28,g25)
    c: PointOnObject(g29,g24)
    c: PointOnObject(g30,g23)
    c: PointOnObject(g31,g22)
    c: PointOnObject(g32,g21)
    c: Equal(g32,g20)
    c: Equal(g32,g27)
    c: Equal(g16,g28)
    c: Equal(g17,g29)
    c: Equal(g18,g30)
    c: Equal(g31,g19)
    c: PointOnObject(g33,g0)
    c: PointOnObject(g34,g0)
    c: PointOnObject(g35,g0)
    c: PointOnObject(g38,g0)
    c: PointOnObject(g37,g0)
    c: PointOnObject(g36,g0)
    c: Symmetric(g38,g23,g30)
    c: Symmetric(g22,g37,g31)
    c: Symmetric(g21,g36,g32)
    c: Symmetric(g26,g35,g27)
    c: Symmetric(g25,g34,g28)
    c: Symmetric(g33,g24,g29)
FEATURE [PartDesign::Pocket] Pocket011
  BaseFeature = -> Pad008
  Direction = (0,0,-1)
  Length = 4.2
  Length2 = 5
  Profile = -> Sketch040
  ReferenceAxis = -> Sketch040 [N_Axis]
  Refine = true
  Reversed = true
  Suppressed = false
  Type = 0
FEATURE [Sketcher::SketchObject] Sketch041
  ArcFitTolerance = 1e-06
  AttachmentOffset = pos=(0,0,5) rot=(0,0,1;1.96349rad)
  AttachmentSupport = -> [XY_Plane006]
  FullyConstrained = false
  MakeInternals = false
  MapMode = 5
  Placement = pos=(0,0,5) rot=(0,0,1;1.96349rad)
  sketch-geometry (20):
    g0: Circle CenterX=0 CenterY=-80 CenterZ=0 NormalX=0 NormalY=0 NormalZ=1 AngleXU=0 Radius=25
    g1: Circle CenterX=0 CenterY=-80 CenterZ=0 NormalX=0 NormalY=0 NormalZ=1 AngleXU=0 Radius=23.7
    g2: LineSegment [constr] StartX=0 StartY=-57 StartZ=0 EndX=0 EndY=-56.3 EndZ=0
    g3: Circle [constr] CenterX=0 CenterY=-56.65 CenterZ=0 NormalX=0 NormalY=0 NormalZ=1 AngleXU=0 Radius=2.6
    g4: LineSegment [constr] StartX=0 StartY=-57 StartZ=0 EndX=0 EndY=-80 EndZ=0
    g5: LineSegment [constr] StartX=0 StartY=-80 StartZ=0 EndX=19.9186 EndY=-68.5 EndZ=0
    g6: LineSegment [constr] StartX=0 StartY=-80 StartZ=0 EndX=19.9186 EndY=-91.5 EndZ=0
    g7: LineSegment [constr] StartX=0 StartY=-80 StartZ=0 EndX=7.2e-15 EndY=-103 EndZ=0
    g8: LineSegment [constr] StartX=0 StartY=-80 StartZ=0 EndX=-19.9186 EndY=-91.5 EndZ=0
    g9: LineSegment [constr] StartX=0 StartY=-80 StartZ=0 EndX=-19.9186 EndY=-68.5 EndZ=0
    g10: GeomPoint [constr] X=20.5248 Y=-68.15 Z=0
    g11: GeomPoint [constr] X=20.5248 Y=-91.85 Z=0
    g12: GeomPoint [constr] X=7.4e-15 Y=-103.7 Z=0
    g13: GeomPoint [constr] X=-20.5248 Y=-91.85 Z=0
    g14: GeomPoint [constr] X=-20.5248 Y=-68.15 Z=0
    g15: Circle [constr] CenterX=-20.2217 CenterY=-68.325 CenterZ=0 NormalX=0 NormalY=0 NormalZ=1 AngleXU=0 Radius=2.6
    g16: Circle [constr] CenterX=-20.2217 CenterY=-91.675 CenterZ=0 NormalX=0 NormalY=0 NormalZ=1 AngleXU=0 Radius=2.6
    g17: Circle [constr] CenterX=7.3e-15 CenterY=-103.35 CenterZ=0 NormalX=0 NormalY=0 NormalZ=1 AngleXU=0 Radius=2.6
    g18: Circle [constr] CenterX=20.2217 CenterY=-91.675 CenterZ=0 NormalX=0 NormalY=0 NormalZ=1 AngleXU=0 Radius=2.6
    g19: Circle [constr] CenterX=20.2217 CenterY=-68.325 CenterZ=0 NormalX=0 NormalY=0 NormalZ=1 AngleXU=0 Radius=2.6
  constraints (42):
    c: Diameter(g0) = 50
    c: PointOnObject(g0,g-2)
    c: DistanceY(g0,g-1) = 80
    c: Diameter(g1) = 47.4
    c: Coincident(g1,g0)
    c: PointOnObject(g2,g1)
    c: Vertical(g2)
    c: PointOnObject(g2,g-2)
    c: Diameter(g3) = 5.2
    c: Symmetric(g2,g2,g3)
    c: Coincident(g4,g2)
    c: Coincident(g4,g0)
    c: Coincident(g5,g0)
    c: Angle(g5,g4) = 1.0472
    c: Coincident(g6,g0)
    c: Coincident(g7,g0)
    c: Coincident(g8,g0)
    c: Coincident(g9,g0)
    c: Angle(g6,g5) = 1.0472
    c: Angle(g7,g6) = 1.0472
    c: Angle(g8,g7) = 1.0472
    c: Angle(g9,g8) = 1.0472
    c: PointOnObject(g10,g1)
    c: PointOnObject(g11,g1)
    c: PointOnObject(g12,g7)
    c: PointOnObject(g13,g8)
    c: PointOnObject(g14,g9)
    c: PointOnObject(g12,g1)
    c: PointOnObject(g13,g1)
    c: PointOnObject(g11,g6)
    c: PointOnObject(g10,g5)
    c: PointOnObject(g14,g1)
    c: Equal(g3,g19)
    c: Equal(g19,g18)
    c: Equal(g18,g17)
    c: Equal(g17,g16)
    c: Equal(g16,g15)
    c: Symmetric(g10,g5,g19)
    c: Symmetric(g11,g6,g18)
    c: Symmetric(g12,g7,g17)
    c: Symmetric(g13,g8,g16)
    c: Symmetric(g9,g14,g15)
FEATURE [PartDesign::Pad] Pad009
  BaseFeature = -> Pocket011
  Direction = (0,0,1)
  Length = 30
  Length2 = 10
  Profile = -> Sketch041
  ReferenceAxis = -> Sketch041 [N_Axis]
  Refine = true
  Suppressed = false
  Type = 0
FEATURE [PartDesign::Chamfer] Chamfer
  Angle = 45
  Base = -> Pad009 [Edge17]
  BaseFeature = -> Pad009
  ChamferType = 1
  FlipDirection = false
  Refine = true
  Size = 4.999
  Size2 = 5
  SupportTransform = false
  Suppressed = false
  UseAllEdges = false
FEATURE [Sketcher::SketchObject] Sketch043
  ArcFitTolerance = 1e-06
  AttachmentOffset = pos=(0,0,27.5) rot=(0,0,1;1.96349rad)
  AttachmentSupport = -> [XY_Plane006]
  FullyConstrained = false
  MakeInternals = false
  MapMode = 5
  Placement = pos=(0,0,27.5) rot=(0,0,1;1.96349rad)
  sketch-geometry (21):
    g0: Circle CenterX=-1e-16 CenterY=-80 CenterZ=0 NormalX=0 NormalY=0 NormalZ=1 AngleXU=0 Radius=25
    g1: Circle [constr] CenterX=-1e-16 CenterY=-80 CenterZ=0 NormalX=0 NormalY=0 NormalZ=1 AngleXU=0 Radius=24
    g2: LineSegment [constr] StartX=0 StartY=-57 StartZ=0 EndX=0 EndY=-56 EndZ=0
    g3: Circle [constr] CenterX=0 CenterY=-56.5 CenterZ=0 NormalX=0 NormalY=0 NormalZ=1 AngleXU=0 Radius=2.6
    g4: LineSegment [constr] StartX=0 StartY=-57 StartZ=0 EndX=-1e-16 EndY=-80 EndZ=0
    g5: LineSegment [constr] StartX=-1e-16 StartY=-80 StartZ=0 EndX=19.9186 EndY=-68.5 EndZ=0
    g6: LineSegment [constr] StartX=-1e-16 StartY=-80 StartZ=0 EndX=19.9186 EndY=-91.5 EndZ=0
    g7: LineSegment [constr] StartX=-1e-16 StartY=-80 StartZ=0 EndX=8.8e-15 EndY=-103 EndZ=0
    g8: LineSegment [constr] StartX=-1e-16 StartY=-80 StartZ=0 EndX=-19.9186 EndY=-91.5 EndZ=0
    g9: LineSegment [constr] StartX=-1e-16 StartY=-80 StartZ=0 EndX=-19.9186 EndY=-68.5 EndZ=0
    g10: GeomPoint [constr] X=20.7846 Y=-68 Z=0
    g11: GeomPoint [constr] X=20.7846 Y=-92 Z=0
    g12: GeomPoint [constr] X=9e-15 Y=-104 Z=0
    g13: GeomPoint [constr] X=-20.7846 Y=-92 Z=0
    g14: GeomPoint [constr] X=-20.7846 Y=-68 Z=0
    g15: Circle [constr] CenterX=-20.3516 CenterY=-68.25 CenterZ=0 NormalX=0 NormalY=0 NormalZ=1 AngleXU=0 Radius=2.6
    g16: Circle [constr] CenterX=-20.3516 CenterY=-91.75 CenterZ=0 NormalX=0 NormalY=0 NormalZ=1 AngleXU=0 Radius=2.6
    g17: Circle [constr] CenterX=8.9e-15 CenterY=-103.5 CenterZ=0 NormalX=0 NormalY=0 NormalZ=1 AngleXU=0 Radius=2.6
    g18: Circle [constr] CenterX=20.3516 CenterY=-91.75 CenterZ=0 NormalX=0 NormalY=0 NormalZ=1 AngleXU=0 Radius=2.6
    g19: Circle [constr] CenterX=20.3516 CenterY=-68.25 CenterZ=0 NormalX=0 NormalY=0 NormalZ=1 AngleXU=0 Radius=2.6
    g20: Circle CenterX=-1e-16 CenterY=-80 CenterZ=0 NormalX=0 NormalY=0 NormalZ=1 AngleXU=0 Radius=26.3
  constraints (44):
    c: Diameter(g0) = 50
    c: PointOnObject(g0,g-2)
    c: DistanceY(g0,g-1) = 80
    c: Diameter(g1) = 48
    c: Coincident(g1,g0)
    c: PointOnObject(g2,g1)
    c: Vertical(g2)
    c: PointOnObject(g2,g-2)
    c: Diameter(g3) = 5.2
    c: Symmetric(g2,g2,g3)
    c: Coincident(g4,g2)
    c: Coincident(g4,g0)
    c: Coincident(g5,g0)
    c: Angle(g5,g4) = 1.0472
    c: Coincident(g6,g0)
    c: Coincident(g7,g0)
    c: Coincident(g8,g0)
    c: Coincident(g9,g0)
    c: Angle(g6,g5) = 1.0472
    c: Angle(g7,g6) = 1.0472
    c: Angle(g8,g7) = 1.0472
    c: Angle(g9,g8) = 1.0472
    c: PointOnObject(g10,g1)
    c: PointOnObject(g11,g1)
    c: PointOnObject(g12,g7)
    c: PointOnObject(g13,g8)
    c: PointOnObject(g14,g9)
    c: PointOnObject(g12,g1)
    c: PointOnObject(g13,g1)
    c: PointOnObject(g11,g6)
    c: PointOnObject(g10,g5)
    c: PointOnObject(g14,g1)
    c: Equal(g3,g19)
    c: Equal(g19,g18)
    c: Equal(g18,g17)
    c: Equal(g17,g16)
    c: Equal(g16,g15)
    c: Symmetric(g10,g5,g19)
    c: Symmetric(g11,g6,g18)
    c: Symmetric(g12,g7,g17)
    c: Symmetric(g13,g8,g16)
    c: Symmetric(g9,g14,g15)
    c: Diameter(g20) = 52.6
    c: Coincident(g20,g0)
FEATURE [PartDesign::Pad] Pad010
  BaseFeature = -> Chamfer
  Direction = (0,0,1)
  Length = 7.5
  Length2 = 10
  Profile = -> Sketch043
  ReferenceAxis = -> Sketch043 [N_Axis]
  Refine = true
  Suppressed = false
  Type = 0
FEATURE [PartDesign::Chamfer] Chamfer003
  Angle = 45
  Base = -> PolarPattern002 [Edge1,Edge6]
  BaseFeature = -> PolarPattern002
  ChamferType = 0
  FlipDirection = false
  Refine = true
  Size = 7.4999
  Size2 = 1
  SupportTransform = false
  Suppressed = false
  UseAllEdges = false
FEATURE [PartDesign::Body] Body
  AllowCompound = false
  Group = -> [Sketch,Pad,Sketch012,Sketch017,Pocket,Pocket001,Sketch020,Sketch027,SubtractiveLoft,Pocket009,PolarPattern,Boolean,Pad007,Sketch034,Pocket007,Sketch035,Pocket008,Sketch036,Sketch037,Sketch038,Pocket010,PolarPattern002,Chamfer003]
  Origin = -> Origin
  Tip = -> Chamfer003
FEATURE [PartDesign::Chamfer] Chamfer001
  Angle = 45
  Base = -> Pad010 [Edge22]
  BaseFeature = -> Pad010
  ChamferType = 0
  FlipDirection = false
  Refine = true
  Size = 1.29
  Size2 = 1
  SupportTransform = false
  Suppressed = false
  UseAllEdges = false
FEATURE [PartDesign::Chamfer] Chamfer002
  Angle = 45
  Base = -> Chamfer001 [Edge11]
  BaseFeature = -> Chamfer001
  ChamferType = 0
  FlipDirection = false
  Refine = true
  Size = 2.59
  Size2 = 1
  SupportTransform = false
  Suppressed = false
  UseAllEdges = false
FEATURE [PartDesign::Body] Body006  label="Hose Adapter"
  AllowCompound = false
  Group = -> [Sketch039,Pad008,Sketch040,Pocket011,Sketch041,Pad009,Chamfer,Sketch043,Pad010,Chamfer001,Chamfer002]
  Origin = -> Origin006
  Placement = pos=(0,0,100) rot=(0,0,1;0rad)
  Tip = -> Chamfer002
